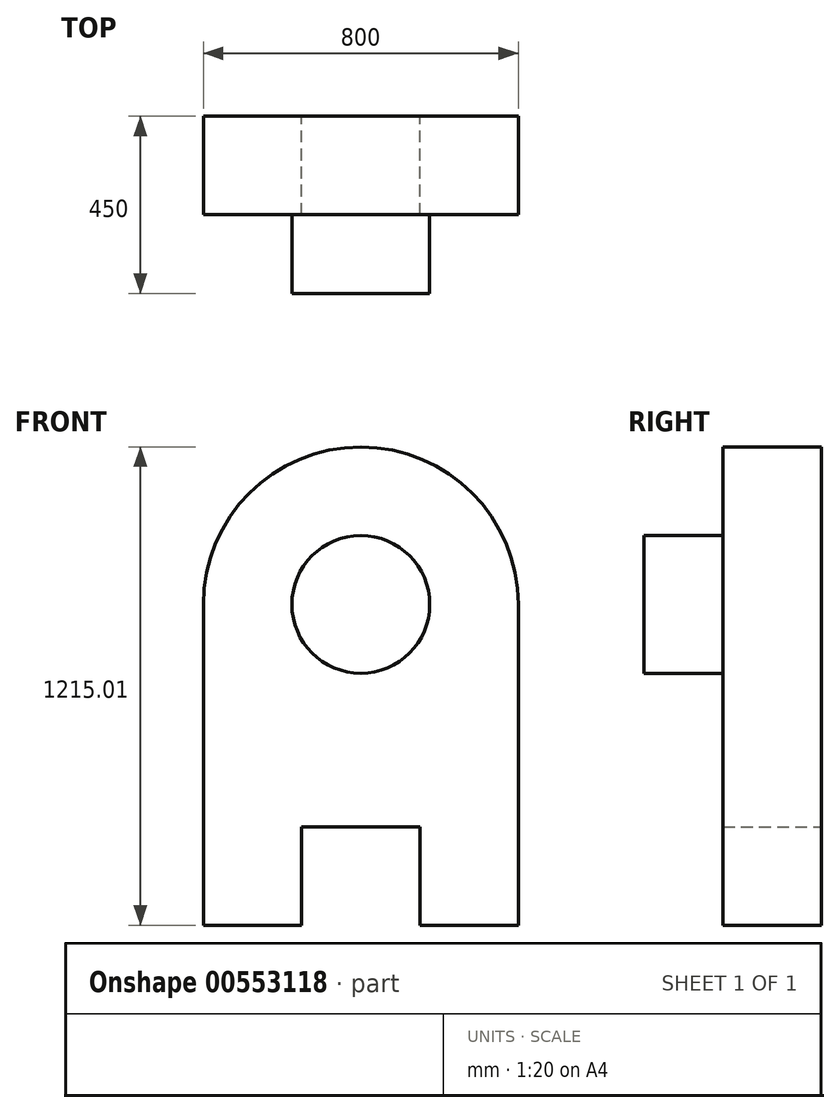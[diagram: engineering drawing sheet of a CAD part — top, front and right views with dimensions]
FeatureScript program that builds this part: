
annotation { "Feature Type Name" : "Feature", "Feature Type Description" : "" }
export const myFeature = defineFeature(function(context is Context, id is Id, definition is map)
    precondition{}
    {
        {
            var Q0;
            Q0=qCreatedBy(makeId("Front.planeOp"),FACE);
            var sketch = newSketch(context, id + "F0", { "sketchPlane" : qUnion([Q0])});
            skArc(sketch, "E0", {"start": v(400, 0) * mm, "mid": v(0, 400) * mm, "end": v(-400, 0) * mm});
            skLineSegment(sketch, "E1.left", {"start": v(-400, 0) * mm, "end": v(-400, -815) * mm});
            skLineSegment(sketch, "E1.right", {"start": v(400, 0) * mm, "end": v(400, -815) * mm});
            skPoint(sketch, "E1.middle", {"position": v(0, -15) * mm});
            skPoint(sketch, "E1.bottom.start.orphan", {"position": v(-400, 785) * mm});
            skPoint(sketch, "E2.orphan", {"position": v(400, 785) * mm});
            skLineSegment(sketch, "E3", {"start": v(400, -815) * mm, "end": v(150, -815) * mm});
            skLineSegment(sketch, "E4", {"start": v(150, -815) * mm, "end": v(150, -565) * mm});
            skLineSegment(sketch, "E5", {"start": v(150, -565) * mm, "end": v(-150, -565) * mm});
            skLineSegment(sketch, "E6", {"start": v(-150, -565) * mm, "end": v(-150, -815) * mm});
            skLineSegment(sketch, "E7", {"start": v(-150, -815) * mm, "end": v(-400, -815) * mm});
            skSolve(sketch);
        }
        {
            var Q0;
            Q0 = qSketchRegion(id + "F0", true);
            extrude(context, id + "F1", {"entities" : qUnion([Q0]), "depth" : 250 * mm, "offsetDistance" : 25 * mm});
        }
        {
            var Q0;
            Q0=makeQuery(id+"F1.opExtrude","CAP_FACE",FACE,{"disambiguationData":[OSD([sQuery(id+"F0.wireOp",EDGE,"E0"),sQuery(id+"F0.wireOp",EDGE,"E1.left"),sQuery(id+"F0.wireOp",EDGE,"E1.right"),sQuery(id+"F0.wireOp",EDGE,"E3"),sQuery(id+"F0.wireOp",EDGE,"E4"),sQuery(id+"F0.wireOp",EDGE,"E5"),sQuery(id+"F0.wireOp",EDGE,"E6"),sQuery(id+"F0.wireOp",EDGE,"E7")])],"isStart":true});
            var sketch = newSketch(context, id + "F2", { "sketchPlane" : qUnion([Q0])});
            skCircle(sketch, "E8", {"center": v(0, 0) * mm, "radius": 175 * mm});
            skSolve(sketch);
        }
        {
            var Q0;
            Q0=makeQuery(id+"F2.imprint","IMPRINT",FACE,{"disambiguationData":[TD([[makeQuery(id+"F2.imprint","IMPRINT",EDGE,{"derivedFrom":sQuery(id+"F2.wireOp",EDGE,"E8")}),1.0]])]});
            extrude(context, id + "F3", {"entities" : qUnion([Q0]), "operationType" : NewBodyOperationType.ADD, "oppositeDirection" : true, "depth" : 200 * mm, "offsetDistance" : 25 * mm});
        }
        {
            var Q0;
            Q0=makeQuery(id+"F1.opExtrude","CAP_FACE",FACE,{"disambiguationData":[OSD([sQuery(id+"F0.wireOp",EDGE,"E0"),sQuery(id+"F0.wireOp",EDGE,"E1.left"),sQuery(id+"F0.wireOp",EDGE,"E1.right"),sQuery(id+"F0.wireOp",EDGE,"E3"),sQuery(id+"F0.wireOp",EDGE,"E4"),sQuery(id+"F0.wireOp",EDGE,"E5"),sQuery(id+"F0.wireOp",EDGE,"E6"),sQuery(id+"F0.wireOp",EDGE,"E7")])],"isStart":false});
            var sketch = newSketch(context, id + "F4", { "sketchPlane" : qUnion([Q0])});
            skCircle(sketch, "E9", {"center": v(0, 0) * mm, "radius": 175 * mm});
            skSolve(sketch);
        }
        {
            var Q0;
            Q0=makeQuery(id+"F4.imprint","IMPRINT",FACE,{"disambiguationData":[TD([[makeQuery(id+"F4.imprint","IMPRINT",EDGE,{"derivedFrom":sQuery(id+"F4.wireOp",EDGE,"E9")}),1.0]])]});
            extrude(context, id + "F5", {"entities" : qUnion([Q0]), "operationType" : NewBodyOperationType.ADD, "depth" : 200 * mm, "offsetDistance" : 25 * mm});
        }
    });
